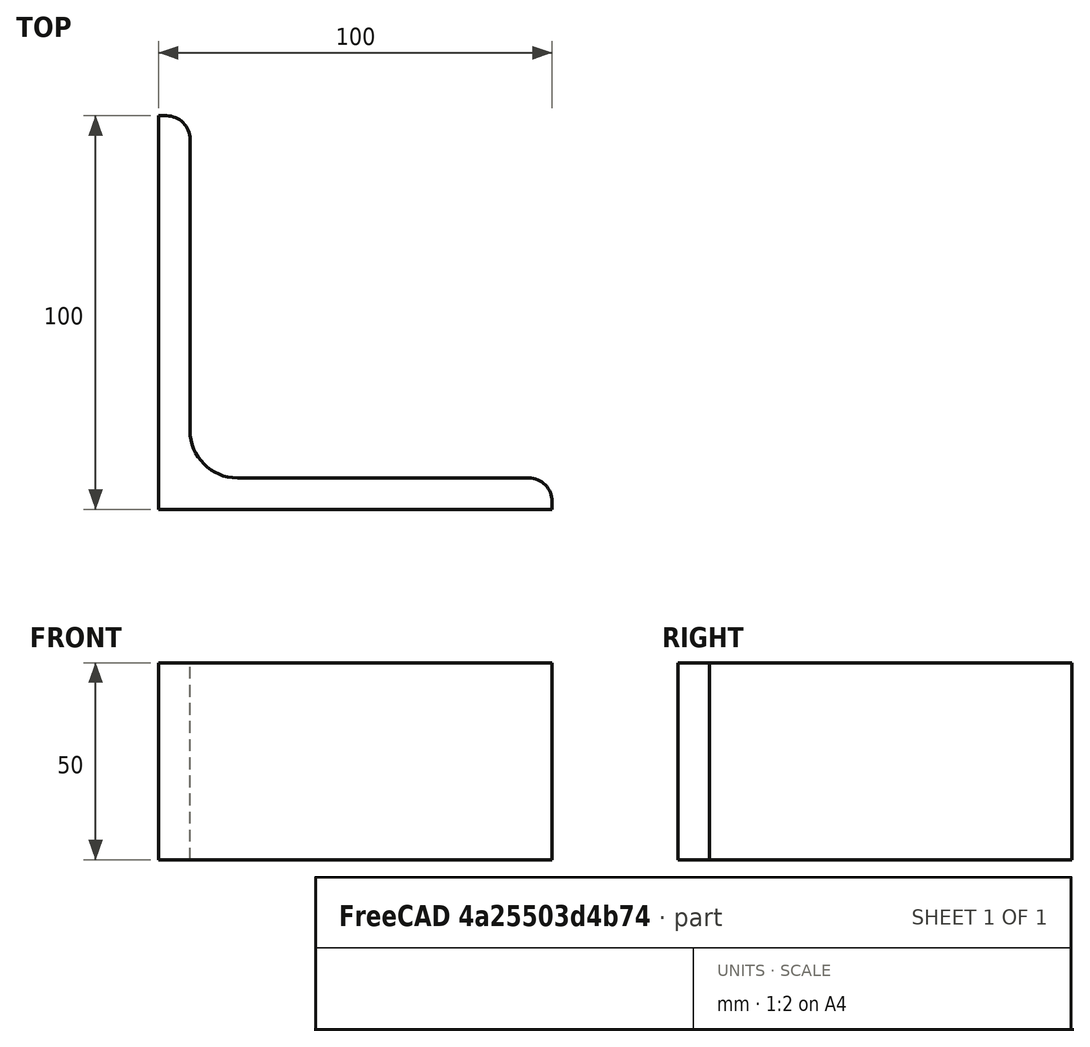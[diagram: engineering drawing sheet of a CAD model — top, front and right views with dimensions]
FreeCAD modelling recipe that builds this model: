
FCSTD DOCUMENT  (FreeCAD 0.15R4671 (Git))
Label: Angle Bar L100x100x8 EN10056 S235JR
License: All rights reserved
LicenseURL: http://en.wikipedia.org/wiki/All_rights_reserved
objects: Sketcher::SketchObject×1, Part::Extrusion×1
note: 2 computed .brp shape members not serialized (recipe doc carries the construction recipe); baked Part::Feature solids carry a one-line shape summary decoded from their .brp

FEATURE [Sketcher::SketchObject] Sketch
  sketch-geometry (9):
    g0: LineSegment StartX=0 StartY=0 StartZ=0 EndX=100 EndY=0 EndZ=0
    g1: LineSegment StartX=100 StartY=0 StartZ=0 EndX=100 EndY=2 EndZ=0
    g2: LineSegment StartX=94 StartY=8 StartZ=0 EndX=20 EndY=8 EndZ=0
    g3: LineSegment StartX=0 StartY=0 StartZ=0 EndX=0 EndY=100 EndZ=0
    g4: LineSegment StartX=0 StartY=100 StartZ=0 EndX=2 EndY=100 EndZ=0
    g5: LineSegment StartX=8 StartY=94 StartZ=0 EndX=8 EndY=20 EndZ=0
    g6: ArcOfCircle CenterX=20 CenterY=20 CenterZ=0 NormalX=0 NormalY=0 NormalZ=1 Radius=12 StartAngle=3.14159 EndAngle=4.71239
    g7: ArcOfCircle CenterX=2 CenterY=94 CenterZ=0 NormalX=0 NormalY=0 NormalZ=1 Radius=6 StartAngle=0 EndAngle=1.5708
    g8: ArcOfCircle CenterX=94 CenterY=2 CenterZ=0 NormalX=0 NormalY=0 NormalZ=1 Radius=6 StartAngle=0 EndAngle=1.5708
  constraints (23):
    c: Coincident(g0,g-1)
    c: Horizontal(g0)
    c: Coincident(g1,g0)
    c: Vertical(g1)
    c: Horizontal(g2)
    c: Coincident(g3,g-1)
    c: Vertical(g3)
    c: Coincident(g4,g3)
    c: Horizontal(g4)
    c: Vertical(g5)
    c: Tangent(g5,g6) = -1.5708
    c: Tangent(g2,g6) = 1.5708
    c: Tangent(g4,g7) = 1.5708
    c: Tangent(g5,g7) = 1.5708
    c: Tangent(g2,g8) = -1.5708
    c: Tangent(g1,g8) = -1.5708
    c: DistanceX(g0) = 100
    c: DistanceY(g3) = 100
    c: DistanceY(g0,g2) = 8
    c: DistanceX(g3,g5) = 8
    c: Radius(g6) = 12
    c: Radius(g8) = 6
    c: Radius(g7) = 6
FEATURE [Part::Extrusion] Extrude  label="Angle Bar L100x100x8 EN10056 S235JR"
  Base = -> Sketch
  Dir = (0,0,50)
  Solid = true
